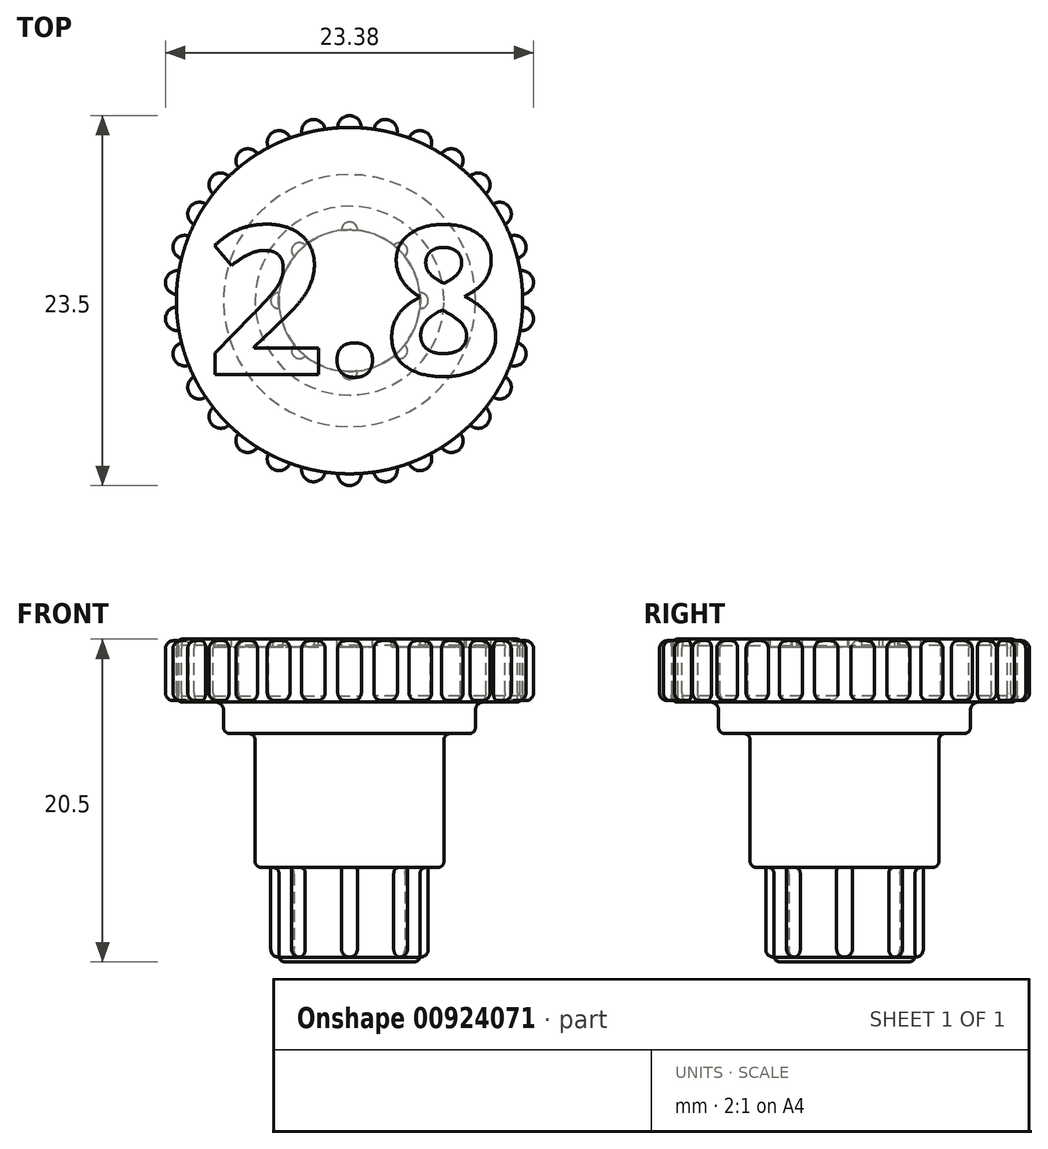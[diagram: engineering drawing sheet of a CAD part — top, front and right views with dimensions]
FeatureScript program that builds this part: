
annotation { "Feature Type Name" : "Feature", "Feature Type Description" : "" }
export const myFeature = defineFeature(function(context is Context, id is Id, definition is map)
    precondition{}
    {
        {
            var Q0;
            Q0=qCreatedBy(makeId("Front.planeOp"),FACE);
            var sketch = newSketch(context, id + "F0", { "sketchPlane" : qUnion([Q0])});
            skLineSegment(sketch, "E0", {"start": v(0, 0) * mm, "end": v(0, 20.5) * mm});
            skLineSegment(sketch, "E1", {"start": v(0, 20.5) * mm, "end": v(11, 20.5) * mm});
            skLineSegment(sketch, "E2", {"start": v(11, 20.5) * mm, "end": v(11, 16.5) * mm});
            skLineSegment(sketch, "E3", {"start": v(11, 16.5) * mm, "end": v(8, 16.5) * mm});
            skLineSegment(sketch, "E4", {"start": v(8, 16.5) * mm, "end": v(8, 14.5) * mm});
            skLineSegment(sketch, "E5", {"start": v(8, 14.5) * mm, "end": v(6, 14.5) * mm});
            skLineSegment(sketch, "E6", {"start": v(6, 14.5) * mm, "end": v(6, 6) * mm});
            skLineSegment(sketch, "E7", {"start": v(6, 6) * mm, "end": v(4.5, 6) * mm});
            skLineSegment(sketch, "E8", {"start": v(4.5, 6) * mm, "end": v(4.5, 0) * mm});
            skLineSegment(sketch, "E9", {"start": v(4.5, 0) * mm, "end": v(0, 0) * mm});
            skSolve(sketch);
        }
        {
            var Q0;
            Q0=makeQuery(id+"F0.imprint","IMPRINT",FACE,{"disambiguationData":[TD([[makeQuery(id+"F0.imprint","IMPRINT",EDGE,{"derivedFrom":sQuery(id+"F0.wireOp",EDGE,"E0")}),-1.0]])]});
            var Q1;
            Q1=sQuery(id+"F0.wireOp",EDGE,"E0");
            revolve(context, id + "F1", {"surfaceOperationType" : NewSurfaceOperationType.NEW, "entities" : qUnion([Q0]), "axis" : qUnion([Q1]), "revolveType" : RevolveType.FULL});
        }
        {
            var Q0;
            Q0=makeQuery(id+"F1.opRevolve","SWEPT_EDGE",EDGE,{"disambiguationData":[OSD([sQuery(id+"F0.wireOp",EDGE,"E3"),sQuery(id+"F0.wireOp",EDGE,"E4")])]});
            fillet(context, id + "F2", {"entities" : qUnion([Q0]), "radius" : 0.5 * mm, "tangentPropagation" : true, "allowEdgeOverflow" : false});
        }
        {
            var Q0;
            Q0=makeQuery(id+"F1.opRevolve","SWEPT_EDGE",EDGE,{"disambiguationData":[OSD([sQuery(id+"F0.wireOp",EDGE,"E2"),sQuery(id+"F0.wireOp",EDGE,"E3")])]});
            var Q1;
            Q1=makeQuery(id+"F1.opRevolve","SWEPT_EDGE",EDGE,{"disambiguationData":[OSD([sQuery(id+"F0.wireOp",EDGE,"E1"),sQuery(id+"F0.wireOp",EDGE,"E2")])]});
            fillet(context, id + "F3", {"entities" : qUnion([Q0, Q1]), "radius" : 0.4 * mm, "tangentPropagation" : true, "allowEdgeOverflow" : false});
        }
        {
            var Q0;
            Q0=makeQuery(id+"F1.opRevolve","SWEPT_FACE",FACE,{"disambiguationData":[OSD([sQuery(id+"F0.wireOp",EDGE,"E1")])]});
            cPlane(context, id + "F4", {"entities" : qUnion([Q0]), "cplaneType" : CPlaneType.OFFSET, "offset" : 0 * mm, "width" : 150 * mm, "height" : 150 * mm});
        }
        {
            var Q0;
            Q0=qCreatedBy(id+"F4.planeOp",FACE);
            var sketch = newSketch(context, id + "F5", { "sketchPlane" : qUnion([Q0])});
            skText(sketch, "E10", { "text": "2.8\n", "fontName": "OpenSans-Bold.ttf"});
            const initialGuessF5  = {"E10": [-0.00908, -0.0047, 1, 0, 0.0095]};
            skSetInitialGuess(sketch, initialGuessF5);
            skSolve(sketch);
        }
        {
            var Q0;
            Q0=qCreatedBy(id+"F4.planeOp",FACE);
            var sketch = newSketch(context, id + "F6", { "sketchPlane" : qUnion([Q0])});
            skCircle(sketch, "E11", {"center": v(0, 0) * mm, "radius": 11 * mm});
            skArc(sketch, "E12", {"start": v(-0.75, -10.97) * mm, "mid": v(0, -11.75) * mm, "end": v(0.75, -10.97) * mm});
            skSolve(sketch);
        }
        {
            var Q0;
            {var subQ0=sQuery(id+"F6.wireOp",EDGE,"E12");Q0=makeQuery(id+"F6.imprint","IMPRINT",FACE,{"disambiguationData":[TD([[makeQuery(id+"F6.imprint","IMPRINT",EDGE,{"derivedFrom":subQ0}),1.0]])]});}
            extrude(context, id + "F7", {"entities" : qUnion([Q0]), "operationType" : NewBodyOperationType.ADD, "oppositeDirection" : true, "depth" : 3.91 * mm, "offsetDistance" : 25 * mm, "hasSecondDirection" : true, "secondDirectionOppositeDirection" : true, "secondDirectionDepth" : 0.1 * mm});
        }
        {
            var Q0;
            Q0=makeQuery(id+"F7.opExtrude","CAP_EDGE",EDGE,{"disambiguationData":[OSD([sQuery(id+"F6.wireOp",EDGE,"E12")])],"isStart":true});
            var Q1;
            Q1=makeQuery(id+"F7.opExtrude","CAP_EDGE",EDGE,{"disambiguationData":[OSD([sQuery(id+"F6.wireOp",EDGE,"E12")])],"isStart":false});
            fillet(context, id + "F8", {"entities" : qUnion([Q0, Q1]), "radius" : 0.5 * mm, "tangentPropagation" : true, "allowEdgeOverflow" : false});
        }
        {
            var Q0;
            Q0=makeQuery(id+"F1.opRevolve","SWEPT_BODY",BODY,{"disambiguationData":[OSD([sQuery(id+"F0.wireOp",EDGE,"E0"),sQuery(id+"F0.wireOp",EDGE,"E1"),sQuery(id+"F0.wireOp",EDGE,"E2"),sQuery(id+"F0.wireOp",EDGE,"E3"),sQuery(id+"F0.wireOp",EDGE,"E4"),sQuery(id+"F0.wireOp",EDGE,"E5"),sQuery(id+"F0.wireOp",EDGE,"E6"),sQuery(id+"F0.wireOp",EDGE,"E7"),sQuery(id+"F0.wireOp",EDGE,"E8"),sQuery(id+"F0.wireOp",EDGE,"E9")])]});
            var Q1;
            Q1=makeQuery(id+"F1.opRevolve","SWEPT_FACE",FACE,{"disambiguationData":[OSD([sQuery(id+"F0.wireOp",EDGE,"E2")])]});
            circularPattern(context, id + "F9", {"operationType" : NewBodyOperationType.ADD, "entities" : qUnion([Q0]), "axis" : qUnion([Q1]), "angle" : 360 * degree, "instanceCount" : 30, "equalSpace" : true, "computeTransformsWithoutBuiltin" : true});
        }
        {
            var Q0;
            Q0=makeQuery(id+"F1.opRevolve","SWEPT_EDGE",EDGE,{"disambiguationData":[OSD([sQuery(id+"F0.wireOp",EDGE,"E6"),sQuery(id+"F0.wireOp",EDGE,"E7")])]});
            var Q1;
            Q1=makeQuery(id+"F1.opRevolve","SWEPT_EDGE",EDGE,{"disambiguationData":[OSD([sQuery(id+"F0.wireOp",EDGE,"E7"),sQuery(id+"F0.wireOp",EDGE,"E8")])]});
            var Q2;
            Q2=makeQuery(id+"F1.opRevolve","SWEPT_EDGE",EDGE,{"disambiguationData":[OSD([sQuery(id+"F0.wireOp",EDGE,"E5"),sQuery(id+"F0.wireOp",EDGE,"E6")])]});
            var Q3;
            Q3=makeQuery(id+"F1.opRevolve","SWEPT_EDGE",EDGE,{"disambiguationData":[OSD([sQuery(id+"F0.wireOp",EDGE,"E4"),sQuery(id+"F0.wireOp",EDGE,"E5")])]});
            var Q4;
            Q4=makeQuery(id+"F1.opRevolve","SWEPT_EDGE",EDGE,{"disambiguationData":[OSD([sQuery(id+"F0.wireOp",EDGE,"E8"),sQuery(id+"F0.wireOp",EDGE,"E9")])]});
            fillet(context, id + "F10", {"entities" : qUnion([Q0, Q1, Q2, Q3, Q4]), "radius" : 0.4 * mm, "tangentPropagation" : true, "allowEdgeOverflow" : false});
        }
        {
            var Q0;
            Q0=makeQuery(id+"F1.opRevolve","SWEPT_FACE",FACE,{"disambiguationData":[OSD([sQuery(id+"F0.wireOp",EDGE,"E9")])]});
            cPlane(context, id + "F11", {"entities" : qUnion([Q0]), "cplaneType" : CPlaneType.OFFSET, "offset" : 0.3 * mm, "oppositeDirection" : true, "width" : 150 * mm, "height" : 150 * mm});
        }
        {
            var Q0;
            Q0=qCreatedBy(id+"F11.planeOp",FACE);
            var sketch = newSketch(context, id + "F12", { "sketchPlane" : qUnion([Q0])});
            skArc(sketch, "E13", {"start": v(-0.5, 4.47) * mm, "mid": v(0, -4.5) * mm, "end": v(0.5, 4.47) * mm});
            skArc(sketch, "E14", {"start": v(0.5, 4.47) * mm, "mid": v(0, 5) * mm, "end": v(-0.5, 4.47) * mm});
            skArc(sketch, "E15.1.0", {"start": v(-2.8, 3.52) * mm, "mid": v(-3.54, 3.54) * mm, "end": v(-3.52, 2.8) * mm});
            skArc(sketch, "E15.2.0", {"start": v(-4.47, 0.5) * mm, "mid": v(-5, 0) * mm, "end": v(-4.47, -0.5) * mm});
            skArc(sketch, "E15.3.0", {"start": v(-3.52, -2.8) * mm, "mid": v(-3.54, -3.54) * mm, "end": v(-2.8, -3.52) * mm});
            skArc(sketch, "E15.4.0", {"start": v(-0.5, -4.47) * mm, "mid": v(0, -5) * mm, "end": v(0.5, -4.47) * mm});
            skArc(sketch, "E15.5.0", {"start": v(2.8, -3.52) * mm, "mid": v(3.54, -3.54) * mm, "end": v(3.52, -2.8) * mm});
            skArc(sketch, "E15.6.0", {"start": v(4.47, -0.5) * mm, "mid": v(5, 0) * mm, "end": v(4.47, 0.5) * mm});
            skArc(sketch, "E15.7.0", {"start": v(3.52, 2.8) * mm, "mid": v(3.54, 3.54) * mm, "end": v(2.8, 3.52) * mm});
            skSolve(sketch);
        }
        {
            var Q0;
            Q0=qSketchRegion(id+"F12",true);
            extrude(context, id + "F13", {"entities" : qUnion([Q0]), "operationType" : NewBodyOperationType.ADD, "oppositeDirection" : true, "depth" : 7 * mm, "offsetDistance" : 25 * mm});
        }
        {
            var Q0;
            Q0=makeQuery(id+"F13.opExtrude","CAP_EDGE",EDGE,{"disambiguationData":[OSD([sQuery(id+"F12.wireOp",EDGE,"E15.7.0")])],"isStart":true});
            var Q1;
            Q1=makeQuery(id+"F13.opExtrude","CAP_EDGE",EDGE,{"disambiguationData":[OSD([sQuery(id+"F12.wireOp",EDGE,"E15.6.0")])],"isStart":true});
            var Q2;
            Q2=makeQuery(id+"F13.opExtrude","CAP_EDGE",EDGE,{"disambiguationData":[OSD([sQuery(id+"F12.wireOp",EDGE,"E15.5.0")])],"isStart":true});
            var Q3;
            Q3=makeQuery(id+"F13.opExtrude","CAP_EDGE",EDGE,{"disambiguationData":[OSD([sQuery(id+"F12.wireOp",EDGE,"E14")])],"isStart":true});
            var Q4;
            Q4=makeQuery(id+"F13.opExtrude","CAP_EDGE",EDGE,{"disambiguationData":[OSD([sQuery(id+"F12.wireOp",EDGE,"E15.1.0")])],"isStart":true});
            var Q5;
            Q5=makeQuery(id+"F13.opExtrude","CAP_EDGE",EDGE,{"disambiguationData":[OSD([sQuery(id+"F12.wireOp",EDGE,"E15.4.0")])],"isStart":true});
            var Q6;
            Q6=makeQuery(id+"F13.opExtrude","CAP_EDGE",EDGE,{"disambiguationData":[OSD([sQuery(id+"F12.wireOp",EDGE,"E15.3.0")])],"isStart":true});
            var Q7;
            Q7=makeQuery(id+"F13.opExtrude","CAP_EDGE",EDGE,{"disambiguationData":[OSD([sQuery(id+"F12.wireOp",EDGE,"E15.2.0")])],"isStart":true});
            fillet(context, id + "F14", {"entities" : qUnion([Q0, Q1, Q2, Q3, Q4, Q5, Q6, Q7]), "radius" : 0.5 * mm, "tangentPropagation" : true, "allowEdgeOverflow" : false});
        }
        {
            var Q0;
            Q0=qSketchRegion(id+"F5",true);
            extrude(context, id + "F15", {"entities" : qUnion([Q0]), "operationType" : NewBodyOperationType.REMOVE, "oppositeDirection" : true, "depth" : 0.5 * mm, "offsetDistance" : 25 * mm});
        }
    });
